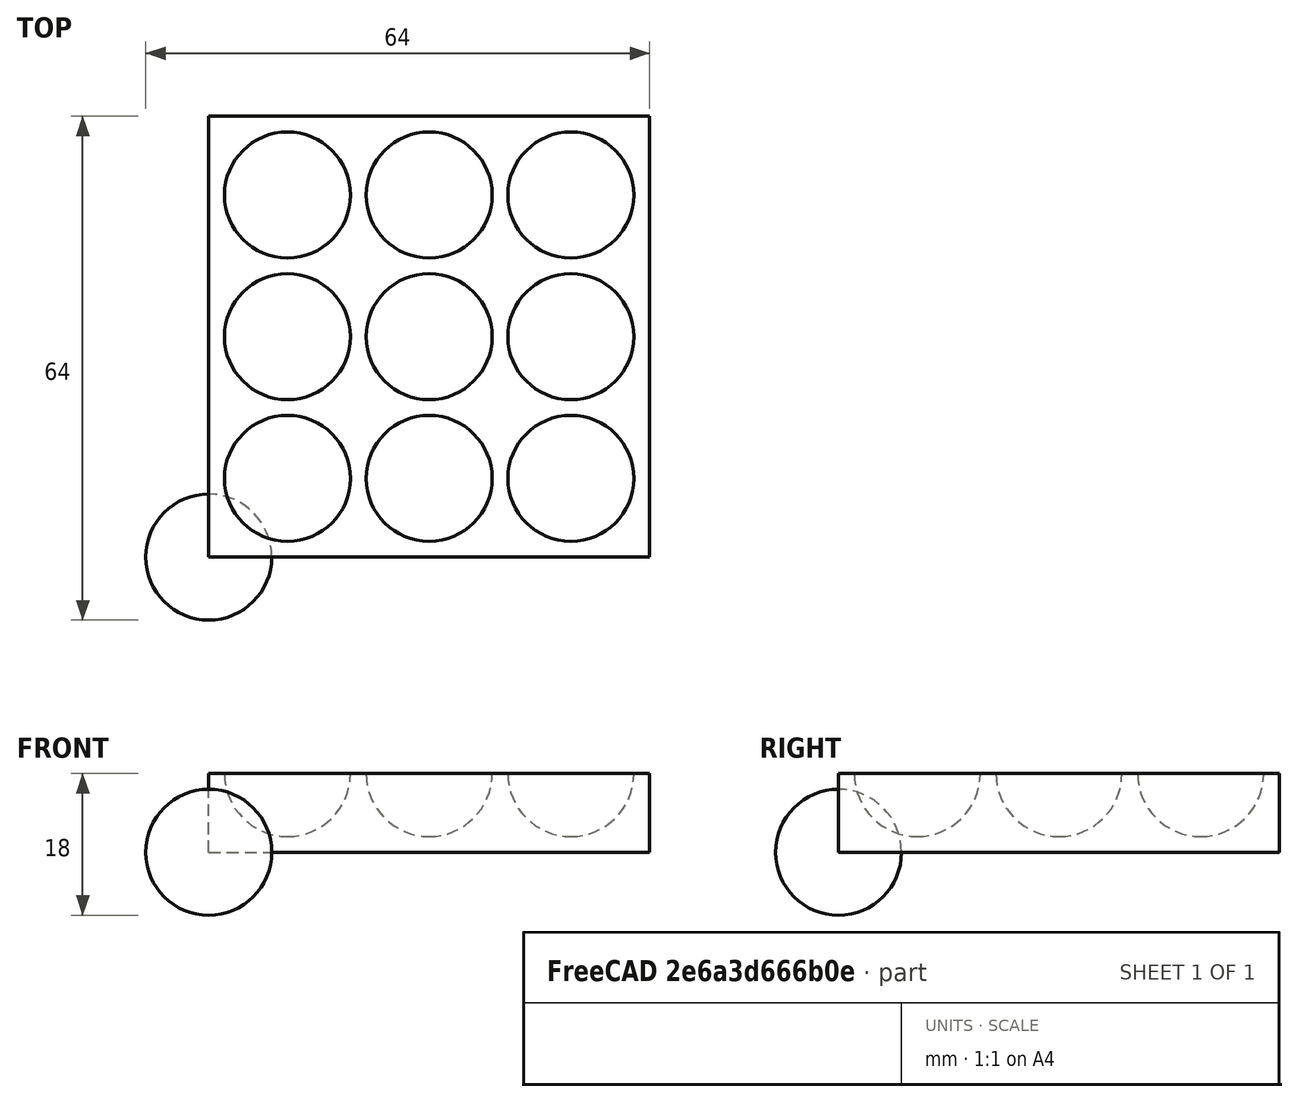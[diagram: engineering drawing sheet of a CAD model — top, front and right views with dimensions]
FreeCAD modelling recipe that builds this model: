
FCSTD DOCUMENT  (FreeCAD 1.0R39319 (Git))
Label: ojt1_t13p01_spheres
License: All rights reserved
LicenseURL: https://en.wikipedia.org/wiki/All_rights_reserved
objects: Part::Sphere×1, Part::FeaturePython×1, Part::Box×1, Part::Cut×1
note: 3 computed .brp shape members not serialized (recipe doc carries the construction recipe); baked Part::Feature solids carry a one-line shape summary decoded from their .brp

FEATURE [Part::Sphere] Sphere  label="Esfera"
  Angle1 = -90
  Angle2 = 90
  Angle3 = 360
  AttacherType = Attacher::AttachEngine3D
  Radius = 8
FEATURE [Part::FeaturePython] Array  # Draft array (typed FeaturePython)
  AlwaysSyncPlacement = false
  Angle = 360
  ArrayType = 0
  Axis = (0,0,1)
  Base = -> Sphere
  Center = (0,0,0)
  Count = 9
  ExpandArray = false
  Fuse = false
  IntervalAxis = (0,0,0)
  IntervalX = (18,0,0)
  IntervalY = (0,18,0)
  IntervalZ = (0,0,100)
  NumberCircles = 3
  NumberPolar = 5
  NumberX = 3
  NumberY = 3
  NumberZ = 1
  Placement = pos=(10,10,10) rot=(0,0,1;0rad)
  PlacementList = 9 placements: [(0,0,0),(0,18,0),(0,36,0),(18,0,0),(18,18,0),(18,36,0),(36,0,0),(36,18,0),(36,36,0)]
  RadialDistance = 50
  ScaleList = (9) [(1,1,1),(1,1,1),(1,1,1),(1,1,1),(1,1,1),(1,1,1),(1,1,1),(1,1,1),(1,1,1)]
  Symmetry = 1
  TangentialDistance = 25
FEATURE [Part::Box] Box  label="Cub"
  AttacherType = Attacher::AttachEngine3D
  Height = 10
  Length = 56
  Width = 56
FEATURE [Part::Cut] Cut
  Base = -> Box
  Refine = true
  Tool = -> Array
